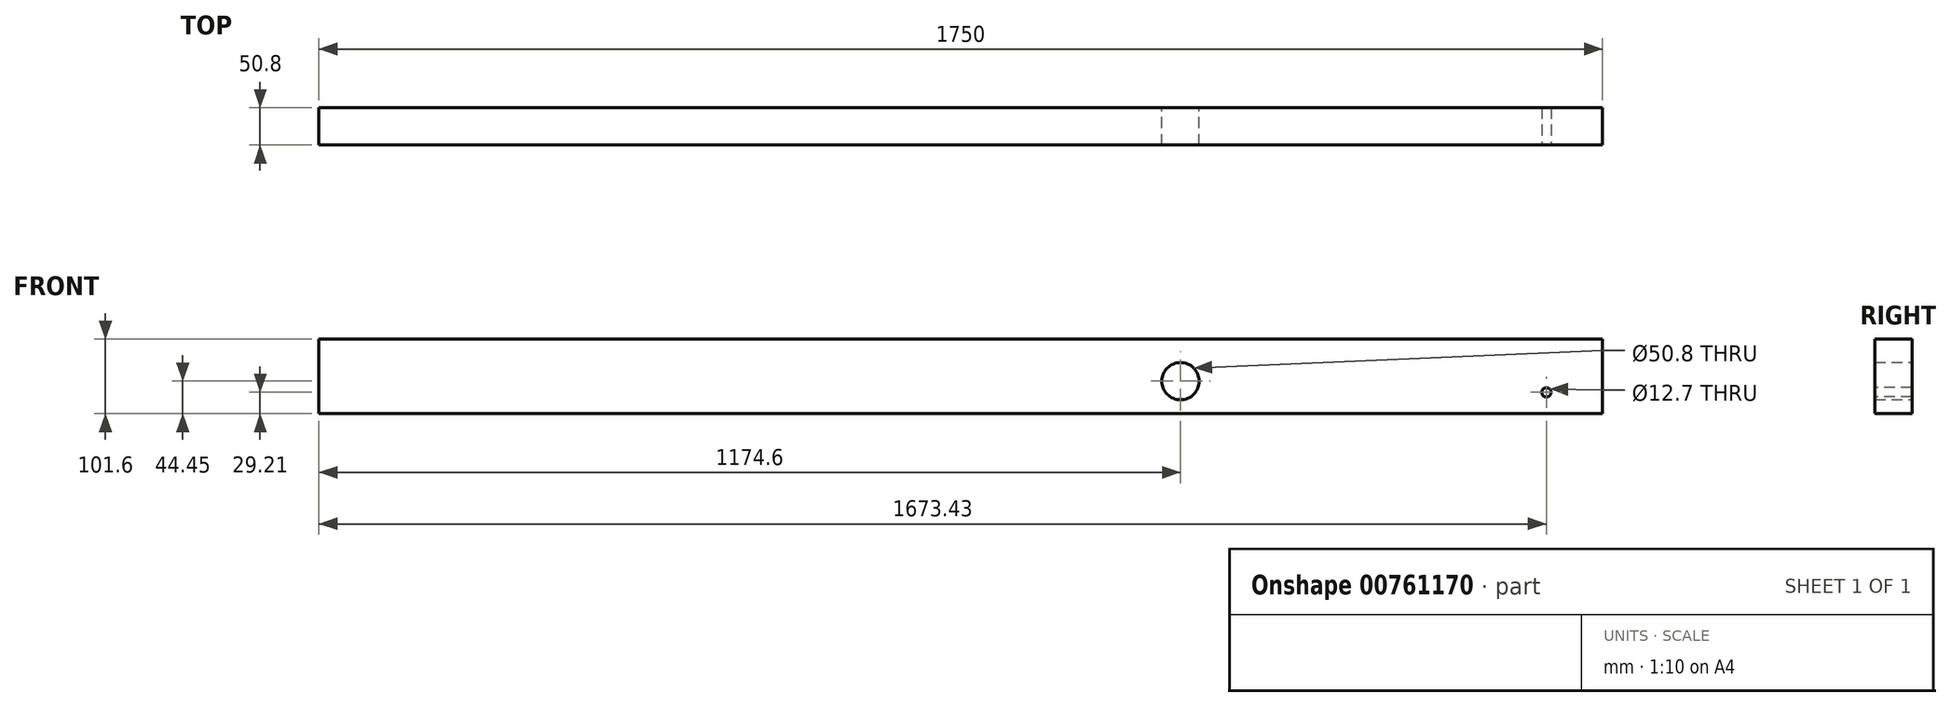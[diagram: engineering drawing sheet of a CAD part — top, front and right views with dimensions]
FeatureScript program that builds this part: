
annotation { "Feature Type Name" : "Feature", "Feature Type Description" : "" }
export const myFeature = defineFeature(function(context is Context, id is Id, definition is map)
    precondition{}
    {
        {
            var Q0;
            Q0=qCreatedBy(makeId("Front.planeOp"),FACE);
            var sketch = newSketch(context, id + "F0", { "sketchPlane" : qUnion([Q0])});
            skLineSegment(sketch, "E0.bottom", {"start": v(-883.72, -133.84) * mm, "end": v(866.28, -133.84) * mm});
            skLineSegment(sketch, "E0.top", {"start": v(-883.72, -235.44) * mm, "end": v(866.28, -235.44) * mm});
            skLineSegment(sketch, "E0.left", {"start": v(-883.72, -133.84) * mm, "end": v(-883.72, -235.44) * mm});
            skLineSegment(sketch, "E0.right", {"start": v(866.28, -133.84) * mm, "end": v(866.28, -235.44) * mm});
            skCircle(sketch, "E1", {"center": v(290.88, -191) * mm, "radius": 25.4 * mm});
            skSolve(sketch);
        }
        {
            var Q0;
            Q0=makeQuery(id+"F0.imprint","IMPRINT",FACE,{"disambiguationData":[TD([[makeQuery(id+"F0.imprint","IMPRINT",EDGE,{"derivedFrom":sQuery(id+"F0.wireOp",EDGE,"E0.bottom")}),-1.0]])]});
            extrude(context, id + "F1", {"entities" : qUnion([Q0]), "depth" : 50.8 * mm, "offsetDistance" : 25.4 * mm});
        }
        {
            var Q0;
            Q0=makeQuery(id+"F1.opExtrude","CAP_FACE",FACE,{"disambiguationData":[OSD([sQuery(id+"F0.wireOp",EDGE,"E0.bottom"),sQuery(id+"F0.wireOp",EDGE,"E0.top"),sQuery(id+"F0.wireOp",EDGE,"E0.left"),sQuery(id+"F0.wireOp",EDGE,"E0.right"),sQuery(id+"F0.wireOp",EDGE,"E1")])],"isStart":false});
            var sketch = newSketch(context, id + "F2", { "sketchPlane" : qUnion([Q0])});
            skCircle(sketch, "E2", {"center": v(789.71, -206.23) * mm, "radius": 6.35 * mm});
            skSolve(sketch);
        }
        {
            var Q0;
            Q0=makeQuery(id+"F2.imprint","IMPRINT",FACE,{"disambiguationData":[TD([[makeQuery(id+"F2.imprint","IMPRINT",EDGE,{"derivedFrom":sQuery(id+"F2.wireOp",EDGE,"E2")}),1.0]])]});
            extrude(context, id + "F3", {"entities" : qUnion([Q0]), "operationType" : NewBodyOperationType.REMOVE, "oppositeDirection" : true, "depth" : 50.8 * mm, "offsetDistance" : 25.4 * mm});
        }
    });
